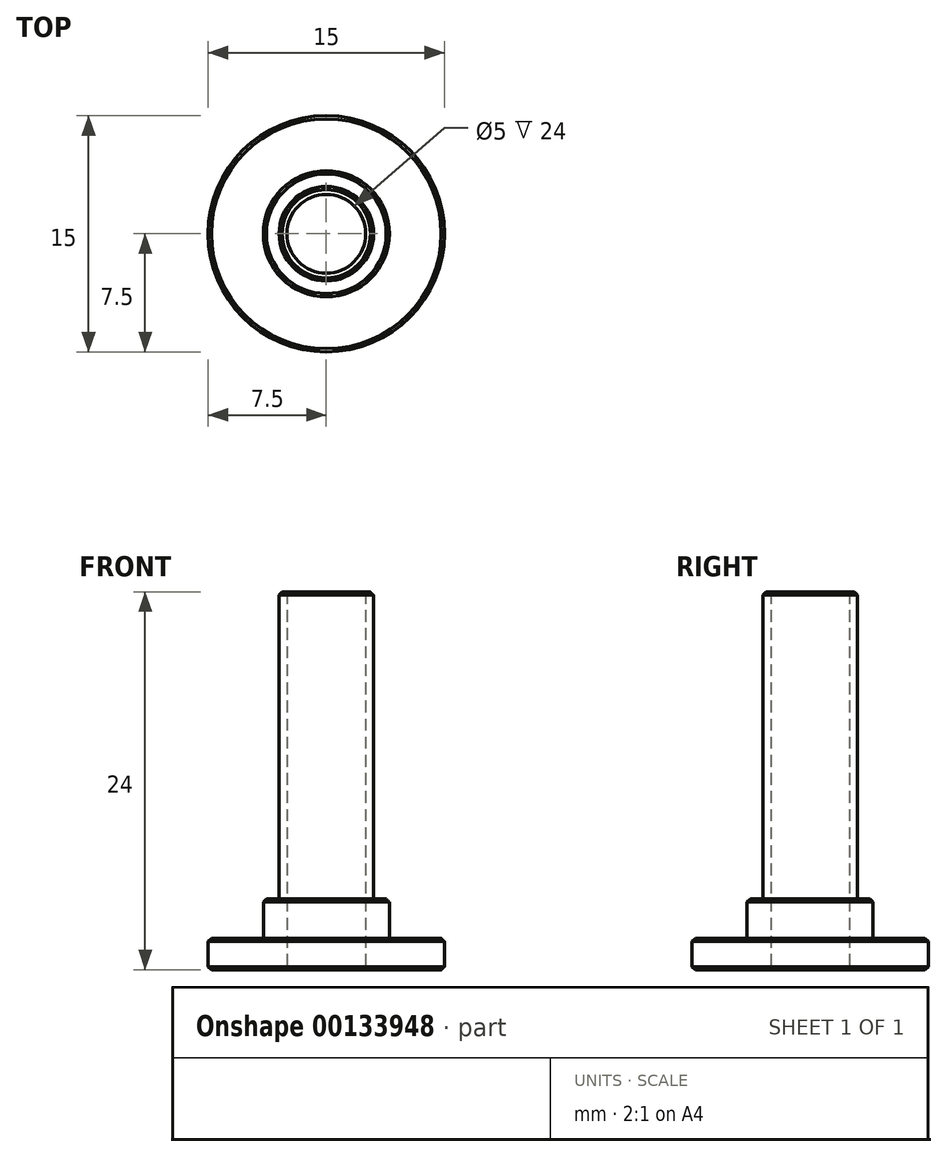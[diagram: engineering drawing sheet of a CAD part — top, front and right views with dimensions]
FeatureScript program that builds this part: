
annotation { "Feature Type Name" : "Feature", "Feature Type Description" : "" }
export const myFeature = defineFeature(function(context is Context, id is Id, definition is map)
    precondition{}
    {
        {
            var Q0;
            Q0=qCreatedBy(makeId("Top.planeOp"),FACE);
            var sketch = newSketch(context, id + "F0", { "sketchPlane" : qUnion([Q0])});
            skCircle(sketch, "E0", {"center": v(0, 0) * mm, "radius": 7.5 * mm});
            skSolve(sketch);
        }
        {
            var Q0;
            Q0=makeQuery(id+"F0.imprint","IMPRINT",FACE,{"disambiguationData":[TD([[makeQuery(id+"F0.imprint","IMPRINT",EDGE,{"derivedFrom":sQuery(id+"F0.wireOp",EDGE,"E0")}),1.0]])]});
            extrude(context, id + "F1", {"entities" : qUnion([Q0]), "depth" : 2 * mm});
        }
        {
            var Q0;
            Q0=makeQuery(id+"F1.opExtrude","CAP_FACE",FACE,{"disambiguationData":[OSD([sQuery(id+"F0.wireOp",EDGE,"E0")])],"isStart":false});
            var sketch = newSketch(context, id + "F2", { "sketchPlane" : qUnion([Q0])});
            skCircle(sketch, "E1", {"center": v(0, 0) * mm, "radius": 3 * mm});
            skSolve(sketch);
        }
        {
            var Q0;
            Q0=makeQuery(id+"F2.imprint","IMPRINT",FACE,{"disambiguationData":[TD([[makeQuery(id+"F2.imprint","IMPRINT",EDGE,{"derivedFrom":sQuery(id+"F2.wireOp",EDGE,"E1")}),1.0]])]});
            extrude(context, id + "F3", {"entities" : qUnion([Q0]), "operationType" : NewBodyOperationType.ADD, "depth" : 22 * mm});
        }
        {
            var Q0;
            Q0=makeQuery(id+"F1.opExtrude","CAP_FACE",FACE,{"disambiguationData":[OSD([sQuery(id+"F0.wireOp",EDGE,"E0")])],"isStart":true});
            var sketch = newSketch(context, id + "F4", { "sketchPlane" : qUnion([Q0])});
            skPoint(sketch, "E2", {"position": v(0, 0) * mm});
            skSolve(sketch);
        }
        {
            var Q0;
            Q0=sQuery(id+"F4.wireOp",VERTEX,"E2");
            var Q1;
            Q1=makeQuery(id+"F1.opExtrude","SWEPT_BODY",BODY,{"disambiguationData":[OSD([sQuery(id+"F0.wireOp",EDGE,"E0")])]});
            hole(context, id + "F5", {"style" : HoleStyle.SIMPLE, "endStyle" : HoleEndStyle.THROUGH, "holeDiameter" : 5 * mm, "startFromSketch" : true, "locations" : qUnion([Q0]), "scope" : qUnion([Q1]), "isTappedThrough" : true});
        }
        {
            var Q0;
            Q0=makeQuery(id+"F1.opExtrude","CAP_FACE",FACE,{"disambiguationData":[OSD([sQuery(id+"F0.wireOp",EDGE,"E0")])],"isStart":false});
            var sketch = newSketch(context, id + "F6", { "sketchPlane" : qUnion([Q0])});
            skCircle(sketch, "E3.0", {"center": v(0, 0) * mm, "radius": 3 * mm});
            skCircle(sketch, "E4", {"center": v(0, 0) * mm, "radius": 4 * mm});
            skSolve(sketch);
        }
        {
            var Q0;
            Q0=makeQuery(id+"F6.imprint","IMPRINT",FACE,{"disambiguationData":[TD([[makeQuery(id+"F6.imprint","IMPRINT",EDGE,{"derivedFrom":sQuery(id+"F6.wireOp",EDGE,"E3.0")}),-1.0]])]});
            extrude(context, id + "F7", {"entities" : qUnion([Q0]), "operationType" : NewBodyOperationType.ADD, "depth" : 2.5 * mm});
        }
        {
            var Q0;
            Q0=makeQuery(id+"F5.hole-0.boolean.opBoolean","COPY",EDGE,{"derivedFrom":makeQuery(id+"F5.hole-0.opRevolve","SWEPT_EDGE",EDGE,{"disambiguationData":[OSD([sQuery(id+"F5.hole-0.sketch.wireOp",EDGE,"core_line_2"),sQuery(id+"F5.hole-0.sketch.wireOp",EDGE,"core_line_3")])]})});
            var Q1;
            Q1=makeQuery(id+"F5.hole-0.boolean.opBoolean","INTERSECT",EDGE,{"derivedFrom":[makeQuery(id+"F3.opExtrude","CAP_FACE",FACE,{"disambiguationData":[OSD([sQuery(id+"F2.wireOp",EDGE,"E1")])],"isStart":false}),makeQuery(id+"F5.hole-0.opRevolve","SWEPT_FACE",FACE,{"disambiguationData":[OSD([sQuery(id+"F5.hole-0.sketch.wireOp",EDGE,"core_line_2")])]})]});
            var Q2;
            Q2=makeQuery(id+"F3.opExtrude","CAP_EDGE",EDGE,{"disambiguationData":[OSD([sQuery(id+"F2.wireOp",EDGE,"E1")])],"isStart":false});
            var Q3;
            Q3=makeQuery(id+"F1.opExtrude","CAP_EDGE",EDGE,{"disambiguationData":[OSD([sQuery(id+"F0.wireOp",EDGE,"E0")])],"isStart":false});
            var Q4;
            Q4=makeQuery(id+"F1.opExtrude","CAP_EDGE",EDGE,{"disambiguationData":[OSD([sQuery(id+"F0.wireOp",EDGE,"E0")])],"isStart":true});
            var Q5;
            Q5=makeQuery(id+"F7.opExtrude","CAP_EDGE",EDGE,{"disambiguationData":[OSD([sQuery(id+"F6.wireOp",EDGE,"E3.0")])],"isStart":false});
            var Q6;
            Q6=makeQuery(id+"F7.opExtrude","CAP_EDGE",EDGE,{"disambiguationData":[OSD([sQuery(id+"F6.wireOp",EDGE,"E4")])],"isStart":false});
            var Q7;
            Q7=makeQuery(id+"F7.opExtrude","CAP_EDGE",EDGE,{"disambiguationData":[OSD([sQuery(id+"F6.wireOp",EDGE,"E4")])],"isStart":true});
            chamfer(context, id + "F8", {"entities" : qUnion([Q0, Q1, Q2, Q3, Q4, Q5, Q6, Q7]), "width" : 0.2 * mm, "tangentPropagation" : true});
        }
    });
